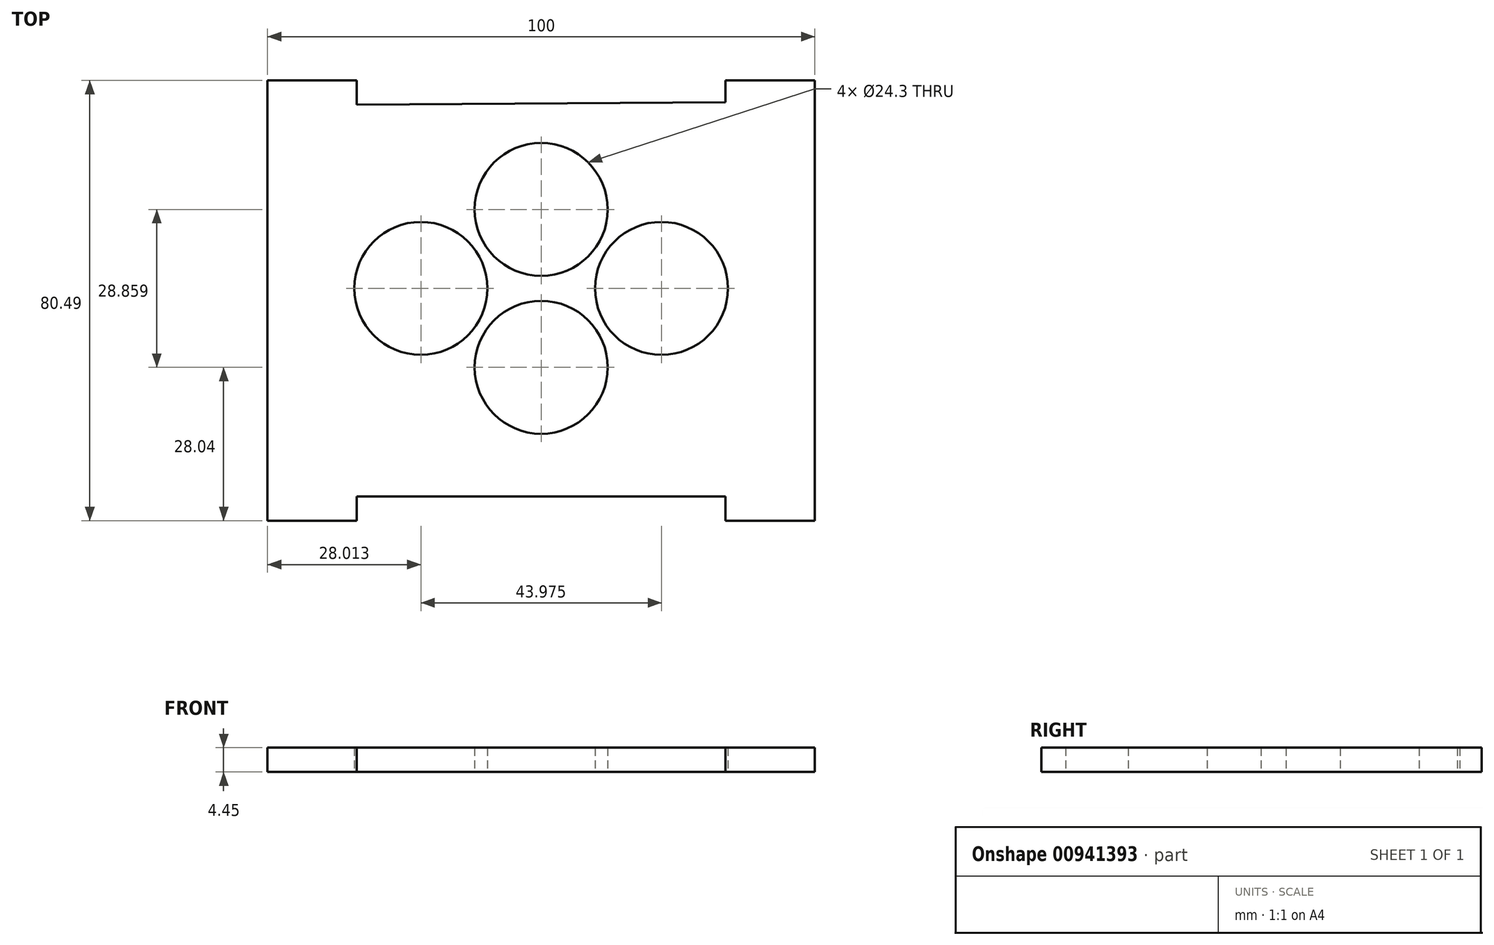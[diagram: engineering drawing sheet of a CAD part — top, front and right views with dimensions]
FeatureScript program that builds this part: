
annotation { "Feature Type Name" : "Feature", "Feature Type Description" : "" }
export const myFeature = defineFeature(function(context is Context, id is Id, definition is map)
    precondition{}
    {
        {
            var Q0;
            Q0=qCreatedBy(makeId("Top.planeOp"),FACE);
            var sketch = newSketch(context, id + "F0", { "sketchPlane" : qUnion([Q0])});
            skLineSegment(sketch, "E0.left", {"start": v(50, -16.64) * mm, "end": v(50, 16.64) * mm});
            skLineSegment(sketch, "E0.right", {"start": v(-50, -33.57) * mm, "end": v(-50, -16.64) * mm});
            skLineSegment(sketch, "E1.right", {"start": v(-33.7, 33.57) * mm, "end": v(-33.7, 38.02) * mm});
            skLineSegment(sketch, "E2.MirrorCS", {"start": v(33.7, 33.57) * mm, "end": v(33.7, 38.02) * mm});
            skLineSegment(sketch, "E3.MirrorCS", {"start": v(50, 33.57) * mm, "end": v(50, 34) * mm});
            skPoint(sketch, "E4.middle", {"position": v(-50, 0) * mm});
            skPoint(sketch, "E5.orphan", {"position": v(-45.55, 16.64) * mm});
            skPoint(sketch, "E6.orphan", {"position": v(-45.55, -16.64) * mm});
            skLineSegment(sketch, "E7.trimOffspring", {"start": v(-50, 16.64) * mm, "end": v(-50, 33.57) * mm});
            skPoint(sketch, "E1.left.end.orphan", {"position": v(-50, 38.02) * mm});
            skPoint(sketch, "E8.MirrorCS.end.orphan", {"position": v(33.7, 38.02) * mm});
            skLineSegment(sketch, "E9", {"start": v(50, 33.57) * mm, "end": v(50, 16.64) * mm});
            skLineSegment(sketch, "E10", {"start": v(50, -16.64) * mm, "end": v(50, -33.57) * mm});
            skLineSegment(sketch, "E11", {"start": v(-50, -16.64) * mm, "end": v(-50, 16.64) * mm});
            skLineSegment(sketch, "E12.right", {"start": v(50, -33.57) * mm, "end": v(50, -38.02) * mm});
            skLineSegment(sketch, "E13.left", {"start": v(-50, -33.57) * mm, "end": v(-50, -38.02) * mm});
            skLineSegment(sketch, "E14.left", {"start": v(-33.7, -38.02) * mm, "end": v(-33.7, -42.47) * mm});
            skLineSegment(sketch, "E14.right", {"start": v(33.7, -38.02) * mm, "end": v(33.7, -42.47) * mm});
            skPoint(sketch, "E15.left.start.orphan", {"position": v(-33.7, -33.57) * mm});
            skPoint(sketch, "E15.top.end.orphan", {"position": v(33.7, -38.02) * mm});
            skLineSegment(sketch, "E16.top", {"start": v(-33.7, 38.02) * mm, "end": v(-50, 38.02) * mm});
            skLineSegment(sketch, "E16.right", {"start": v(-50, 33.57) * mm, "end": v(-50, 38.02) * mm});
            skLineSegment(sketch, "E17.bottom", {"start": v(33.7, 38.02) * mm, "end": v(50, 38.02) * mm});
            skLineSegment(sketch, "E17.left", {"start": v(33.7, 38.02) * mm, "end": v(33.7, 34) * mm});
            skLineSegment(sketch, "E17.right", {"start": v(50, 38.02) * mm, "end": v(50, 34) * mm});
            skLineSegment(sketch, "E18.top", {"start": v(50, -42.47) * mm, "end": v(33.7, -42.47) * mm});
            skLineSegment(sketch, "E18.left", {"start": v(50, -38.02) * mm, "end": v(50, -42.47) * mm});
            skLineSegment(sketch, "E19.top", {"start": v(-50, -42.47) * mm, "end": v(-33.7, -42.47) * mm});
            skLineSegment(sketch, "E19.left", {"start": v(-50, -38.02) * mm, "end": v(-50, -42.47) * mm});
            skLineSegment(sketch, "E20", {"start": v(-33.7, 33.57) * mm, "end": v(33.7, 34) * mm});
            skLineSegment(sketch, "E21", {"start": v(-33.7, -38.02) * mm, "end": v(33.7, -38.02) * mm});
            skPoint(sketch, "E22.MirrorCS.start.orphan", {"position": v(-33.7, 38.02) * mm});
            skCircle(sketch, "E23", {"center": v(0, 14.43) * mm, "radius": 12.15 * mm});
            skCircle(sketch, "E24.MirrorC", {"center": v(0, -14.43) * mm, "radius": 12.15 * mm});
            skCircle(sketch, "E25", {"center": v(-21.99, 0) * mm, "radius": 12.15 * mm});
            skCircle(sketch, "E26.MirrorC", {"center": v(21.99, 0) * mm, "radius": 12.15 * mm});
            skSolve(sketch);
        }
        {
            var Q0;
            Q0=makeQuery(id+"F0.imprint","IMPRINT",FACE,{"disambiguationData":[TD([[makeQuery(id+"F0.imprint","IMPRINT",EDGE,{"derivedFrom":sQuery(id+"F0.wireOp",EDGE,"E0.left")}),1.0]])]});
            extrude(context, id + "F1", {"entities" : qUnion([Q0]), "depth" : 4.45 * mm, "offsetDistance" : 25 * mm});
        }
    });
